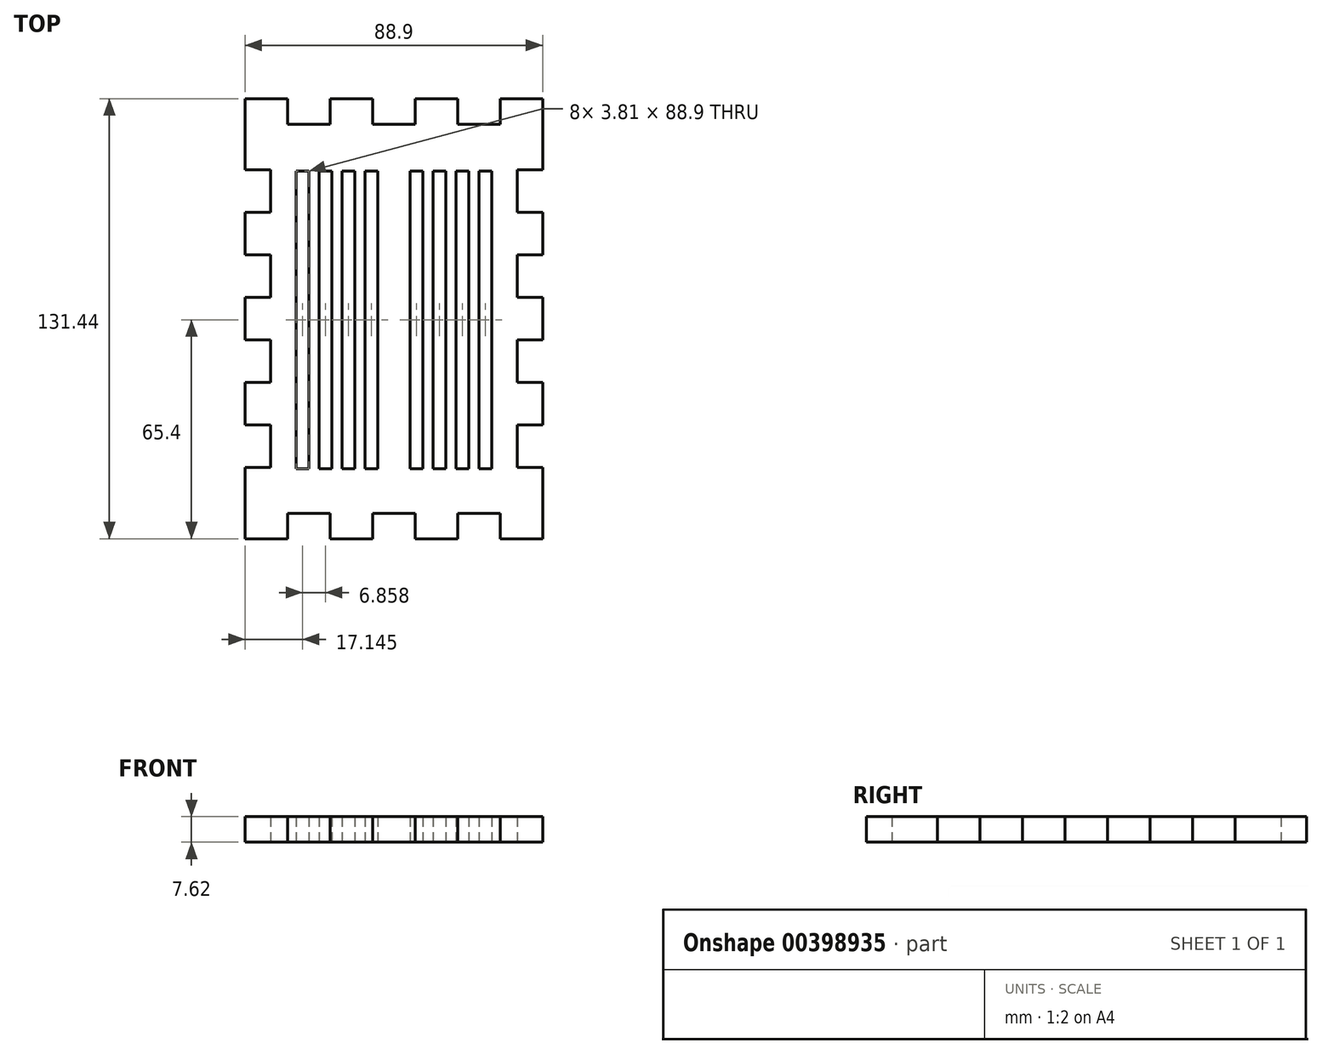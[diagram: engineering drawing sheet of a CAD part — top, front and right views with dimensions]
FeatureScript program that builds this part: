
annotation { "Feature Type Name" : "Feature", "Feature Type Description" : "" }
export const myFeature = defineFeature(function(context is Context, id is Id, definition is map)
    precondition{}
    {
        {
            var Q0;
            Q0=qCreatedBy(makeId("Top.planeOp"),FACE);
            var sketch = newSketch(context, id + "F0", { "sketchPlane" : qUnion([Q0])});
            skLineSegment(sketch, "E0.bottom", {"start": v(0, 0) * mm, "end": v(12.7, 0) * mm});
            skLineSegment(sketch, "E0.left", {"start": v(0, 0) * mm, "end": v(0, -21.27) * mm});
            skLineSegment(sketch, "E1", {"start": v(12.7, 0) * mm, "end": v(12.7, -7.62) * mm});
            skLineSegment(sketch, "E2", {"start": v(12.7, -7.62) * mm, "end": v(25.4, -7.62) * mm});
            skLineSegment(sketch, "E3", {"start": v(25.4, -7.62) * mm, "end": v(25.4, 0) * mm});
            skLineSegment(sketch, "E4", {"start": v(25.4, 0) * mm, "end": v(38.1, 0) * mm});
            skLineSegment(sketch, "E5", {"start": v(38.1, 0) * mm, "end": v(38.1, -7.62) * mm});
            skLineSegment(sketch, "E6", {"start": v(38.1, -7.62) * mm, "end": v(50.8, -7.62) * mm});
            skLineSegment(sketch, "E7", {"start": v(50.8, -7.62) * mm, "end": v(50.8, 0) * mm});
            skLineSegment(sketch, "E8", {"start": v(50.8, 0) * mm, "end": v(63.5, 0) * mm});
            skLineSegment(sketch, "E9", {"start": v(63.5, 0) * mm, "end": v(63.5, -7.62) * mm});
            skLineSegment(sketch, "E10", {"start": v(63.5, -7.62) * mm, "end": v(76.2, -7.62) * mm});
            skLineSegment(sketch, "E11", {"start": v(76.2, -7.62) * mm, "end": v(76.2, 0) * mm});
            skLineSegment(sketch, "E12.trimOffspring", {"start": v(76.2, 0) * mm, "end": v(88.9, 0) * mm});
            skLineSegment(sketch, "E13", {"start": v(0, -21.27) * mm, "end": v(7.62, -21.27) * mm});
            skLineSegment(sketch, "E14", {"start": v(7.62, -21.27) * mm, "end": v(7.62, -33.97) * mm});
            skLineSegment(sketch, "E15", {"start": v(7.62, -33.97) * mm, "end": v(0, -33.97) * mm});
            skLineSegment(sketch, "E16", {"start": v(0, -33.97) * mm, "end": v(0, -46.67) * mm});
            skLineSegment(sketch, "E17", {"start": v(0, -46.67) * mm, "end": v(7.62, -46.67) * mm});
            skLineSegment(sketch, "E18", {"start": v(7.62, -46.67) * mm, "end": v(7.62, -59.37) * mm});
            skLineSegment(sketch, "E19", {"start": v(7.62, -59.37) * mm, "end": v(0, -59.37) * mm});
            skLineSegment(sketch, "E20", {"start": v(0, -59.37) * mm, "end": v(0, -72.07) * mm});
            skLineSegment(sketch, "E21", {"start": v(0, -72.07) * mm, "end": v(7.62, -72.07) * mm});
            skLineSegment(sketch, "E22", {"start": v(7.62, -72.07) * mm, "end": v(7.62, -84.77) * mm});
            skLineSegment(sketch, "E23", {"start": v(7.62, -84.77) * mm, "end": v(0, -84.77) * mm});
            skLineSegment(sketch, "E24", {"start": v(0, -84.77) * mm, "end": v(0, -97.47) * mm});
            skLineSegment(sketch, "E25", {"start": v(0, -97.47) * mm, "end": v(7.62, -97.47) * mm});
            skLineSegment(sketch, "E26", {"start": v(7.62, -97.47) * mm, "end": v(7.62, -110.17) * mm});
            skLineSegment(sketch, "E27", {"start": v(7.62, -110.17) * mm, "end": v(0, -110.17) * mm});
            skLineSegment(sketch, "E28.trimOffspring", {"start": v(0, -110.17) * mm, "end": v(0, -131.46) * mm});
            skLineSegment(sketch, "E29", {"start": v(44.45, -7.62) * mm, "end": v(44.45, -50.1) * mm, "construction": true});
            skLineSegment(sketch, "E30.MirrorCS", {"start": v(88.9, 0) * mm, "end": v(88.9, -21.27) * mm});
            skLineSegment(sketch, "E31.MirrorCS", {"start": v(88.9, -21.27) * mm, "end": v(81.28, -21.27) * mm});
            skLineSegment(sketch, "E32.MirrorCS", {"start": v(81.28, -21.27) * mm, "end": v(81.28, -33.97) * mm});
            skLineSegment(sketch, "E33.MirrorCS", {"start": v(81.28, -33.97) * mm, "end": v(88.9, -33.97) * mm});
            skLineSegment(sketch, "E34.MirrorCS", {"start": v(88.9, -33.97) * mm, "end": v(88.9, -46.67) * mm});
            skLineSegment(sketch, "E35.MirrorCS", {"start": v(88.9, -46.67) * mm, "end": v(81.28, -46.67) * mm});
            skLineSegment(sketch, "E36.MirrorCS", {"start": v(81.28, -46.67) * mm, "end": v(81.28, -59.37) * mm});
            skLineSegment(sketch, "E37.MirrorCS", {"start": v(81.28, -59.37) * mm, "end": v(88.9, -59.37) * mm});
            skLineSegment(sketch, "E38.MirrorCS", {"start": v(88.9, -59.37) * mm, "end": v(88.9, -72.07) * mm});
            skLineSegment(sketch, "E39.MirrorCS", {"start": v(88.9, -72.07) * mm, "end": v(81.28, -72.07) * mm});
            skLineSegment(sketch, "E40.MirrorCS", {"start": v(81.28, -72.07) * mm, "end": v(81.28, -84.77) * mm});
            skLineSegment(sketch, "E41.MirrorCS", {"start": v(81.28, -84.77) * mm, "end": v(88.9, -84.77) * mm});
            skLineSegment(sketch, "E42.MirrorCS", {"start": v(88.9, -84.77) * mm, "end": v(88.9, -97.47) * mm});
            skLineSegment(sketch, "E43.MirrorCS", {"start": v(88.9, -97.47) * mm, "end": v(81.28, -97.47) * mm});
            skLineSegment(sketch, "E44.MirrorCS", {"start": v(81.28, -97.47) * mm, "end": v(81.28, -110.17) * mm});
            skLineSegment(sketch, "E45.MirrorCS", {"start": v(88.9, -110.17) * mm, "end": v(88.9, -131.46) * mm});
            skLineSegment(sketch, "E46.MirrorCS", {"start": v(81.28, -110.17) * mm, "end": v(88.9, -110.17) * mm});
            skLineSegment(sketch, "E47", {"start": v(0, -65.72) * mm, "end": v(37.66, -65.72) * mm, "construction": true});
            skPoint(sketch, "E47.endSnap0", {"position": v(0, -65.72) * mm});
            skLineSegment(sketch, "E48.MirrorCS", {"start": v(0, -131.45) * mm, "end": v(12.7, -131.45) * mm});
            skLineSegment(sketch, "E49.MirrorCS", {"start": v(12.7, -131.45) * mm, "end": v(12.7, -123.83) * mm});
            skLineSegment(sketch, "E50.MirrorCS", {"start": v(12.7, -123.83) * mm, "end": v(25.4, -123.83) * mm});
            skLineSegment(sketch, "E51.MirrorCS", {"start": v(25.4, -123.83) * mm, "end": v(25.4, -131.45) * mm});
            skLineSegment(sketch, "E52.MirrorCS", {"start": v(25.4, -131.45) * mm, "end": v(38.1, -131.45) * mm});
            skLineSegment(sketch, "E53.MirrorCS", {"start": v(38.1, -131.45) * mm, "end": v(38.1, -123.83) * mm});
            skLineSegment(sketch, "E54.MirrorCS", {"start": v(38.1, -123.83) * mm, "end": v(50.8, -123.83) * mm});
            skLineSegment(sketch, "E55.MirrorCS", {"start": v(50.8, -123.83) * mm, "end": v(50.8, -131.45) * mm});
            skLineSegment(sketch, "E56.MirrorCS", {"start": v(50.8, -131.45) * mm, "end": v(63.5, -131.45) * mm});
            skLineSegment(sketch, "E57.MirrorCS", {"start": v(63.5, -131.45) * mm, "end": v(63.5, -123.83) * mm});
            skLineSegment(sketch, "E58.MirrorCS", {"start": v(63.5, -123.83) * mm, "end": v(76.2, -123.83) * mm});
            skLineSegment(sketch, "E59.MirrorCS", {"start": v(76.2, -123.83) * mm, "end": v(76.2, -131.45) * mm});
            skLineSegment(sketch, "E60.MirrorCS", {"start": v(76.2, -131.45) * mm, "end": v(88.9, -131.45) * mm});
            skLineSegment(sketch, "E61.bottom", {"start": v(-84.62, -3.32) * mm, "end": v(-109.67, -3.32) * mm, "construction": true});
            skLineSegment(sketch, "E61.top", {"start": v(-84.62, -131.12) * mm, "end": v(-109.67, -131.12) * mm, "construction": true});
            skLineSegment(sketch, "E61.left", {"start": v(-84.62, -3.32) * mm, "end": v(-84.62, -131.12) * mm, "construction": true});
            skLineSegment(sketch, "E61.right", {"start": v(-109.67, -3.32) * mm, "end": v(-109.67, -131.12) * mm, "construction": true});
            skLineSegment(sketch, "E62", {"start": v(-90.88, -3.32) * mm, "end": v(-90.88, -25.05) * mm, "construction": true});
            skLineSegment(sketch, "E63", {"start": v(-90.88, -25.05) * mm, "end": v(-84.62, -25.05) * mm, "construction": true});
            skLineSegment(sketch, "E64", {"start": v(-84.62, -25.05) * mm, "end": v(-84.62, -37.94) * mm, "construction": true});
            skLineSegment(sketch, "E65", {"start": v(-84.62, -37.94) * mm, "end": v(-91.99, -37.94) * mm, "construction": true});
            skLineSegment(sketch, "E66", {"start": v(-91.99, -37.94) * mm, "end": v(-91.99, -51.2) * mm, "construction": true});
            skLineSegment(sketch, "E67", {"start": v(-91.99, -51.2) * mm, "end": v(-84.62, -51.2) * mm, "construction": true});
            skLineSegment(sketch, "E68", {"start": v(-84.62, -51.2) * mm, "end": v(-84.62, -67.22) * mm, "construction": true});
            skLineSegment(sketch, "E69.bottom", {"start": v(15.24, -21.6) * mm, "end": v(19.05, -21.6) * mm});
            skLineSegment(sketch, "E69.top", {"start": v(15.24, -110.5) * mm, "end": v(19.05, -110.5) * mm});
            skLineSegment(sketch, "E69.left", {"start": v(15.24, -21.6) * mm, "end": v(15.24, -110.5) * mm});
            skLineSegment(sketch, "E69.right", {"start": v(19.05, -21.6) * mm, "end": v(19.05, -110.5) * mm});
            skLineSegment(sketch, "E70.bottom", {"start": v(25.9, -21.6) * mm, "end": v(22.1, -21.6) * mm});
            skLineSegment(sketch, "E70.top", {"start": v(25.9, -110.5) * mm, "end": v(22.1, -110.5) * mm});
            skLineSegment(sketch, "E70.left", {"start": v(25.9, -21.6) * mm, "end": v(25.9, -110.5) * mm});
            skLineSegment(sketch, "E70.right", {"start": v(22.1, -21.6) * mm, "end": v(22.1, -110.5) * mm});
            skLineSegment(sketch, "E71.bottom", {"start": v(32.77, -21.6) * mm, "end": v(28.96, -21.6) * mm});
            skLineSegment(sketch, "E71.top", {"start": v(32.77, -110.5) * mm, "end": v(28.96, -110.5) * mm});
            skLineSegment(sketch, "E71.left", {"start": v(32.77, -21.6) * mm, "end": v(32.77, -110.5) * mm});
            skLineSegment(sketch, "E71.right", {"start": v(28.96, -21.6) * mm, "end": v(28.96, -110.5) * mm});
            skLineSegment(sketch, "E72.bottom", {"start": v(39.62, -21.6) * mm, "end": v(35.81, -21.6) * mm});
            skLineSegment(sketch, "E72.top", {"start": v(39.62, -110.5) * mm, "end": v(35.81, -110.5) * mm});
            skLineSegment(sketch, "E72.left", {"start": v(39.62, -21.6) * mm, "end": v(39.62, -110.5) * mm});
            skLineSegment(sketch, "E72.right", {"start": v(35.81, -21.6) * mm, "end": v(35.81, -110.5) * mm});
            skLineSegment(sketch, "E73.MirrorCS", {"start": v(49.28, -21.6) * mm, "end": v(49.28, -110.5) * mm});
            skLineSegment(sketch, "E74.MirrorCS", {"start": v(49.28, -21.6) * mm, "end": v(53.09, -21.6) * mm});
            skLineSegment(sketch, "E75.MirrorCS", {"start": v(53.09, -21.6) * mm, "end": v(53.09, -110.5) * mm});
            skLineSegment(sketch, "E76.MirrorCS", {"start": v(56.13, -21.6) * mm, "end": v(56.13, -110.5) * mm});
            skLineSegment(sketch, "E77.MirrorCS", {"start": v(56.13, -21.6) * mm, "end": v(59.94, -21.6) * mm});
            skLineSegment(sketch, "E78.MirrorCS", {"start": v(59.94, -21.6) * mm, "end": v(59.94, -110.5) * mm});
            skLineSegment(sketch, "E79.MirrorCS", {"start": v(63, -21.6) * mm, "end": v(63, -110.5) * mm});
            skLineSegment(sketch, "E80.MirrorCS", {"start": v(66.8, -21.6) * mm, "end": v(66.8, -110.5) * mm});
            skLineSegment(sketch, "E81.MirrorCS", {"start": v(63, -21.6) * mm, "end": v(66.8, -21.6) * mm});
            skLineSegment(sketch, "E82.MirrorCS", {"start": v(69.85, -21.6) * mm, "end": v(69.85, -110.5) * mm});
            skLineSegment(sketch, "E83.MirrorCS", {"start": v(73.66, -21.6) * mm, "end": v(69.85, -21.6) * mm});
            skLineSegment(sketch, "E84.MirrorCS", {"start": v(73.66, -21.6) * mm, "end": v(73.66, -110.5) * mm});
            skLineSegment(sketch, "E85.MirrorCS", {"start": v(49.28, -110.5) * mm, "end": v(53.09, -110.5) * mm});
            skLineSegment(sketch, "E86.MirrorCS", {"start": v(56.13, -110.5) * mm, "end": v(59.94, -110.5) * mm});
            skLineSegment(sketch, "E87.MirrorCS", {"start": v(63, -110.5) * mm, "end": v(66.8, -110.5) * mm});
            skLineSegment(sketch, "E88.MirrorCS", {"start": v(73.66, -110.5) * mm, "end": v(69.85, -110.5) * mm});
            skSolve(sketch);
        }
        {
            var Q0;
            Q0=makeQuery(id+"F0.imprint","IMPRINT",FACE,{"disambiguationData":[TD([[makeQuery(id+"F0.imprint","IMPRINT",EDGE,{"derivedFrom":sQuery(id+"F0.wireOp",EDGE,"E0.bottom")}),-1.0]])]});
            extrude(context, id + "F1", {"entities" : qUnion([Q0]), "depth" : 7.62 * mm, "offsetDistance" : 25.4 * mm});
        }
    });
